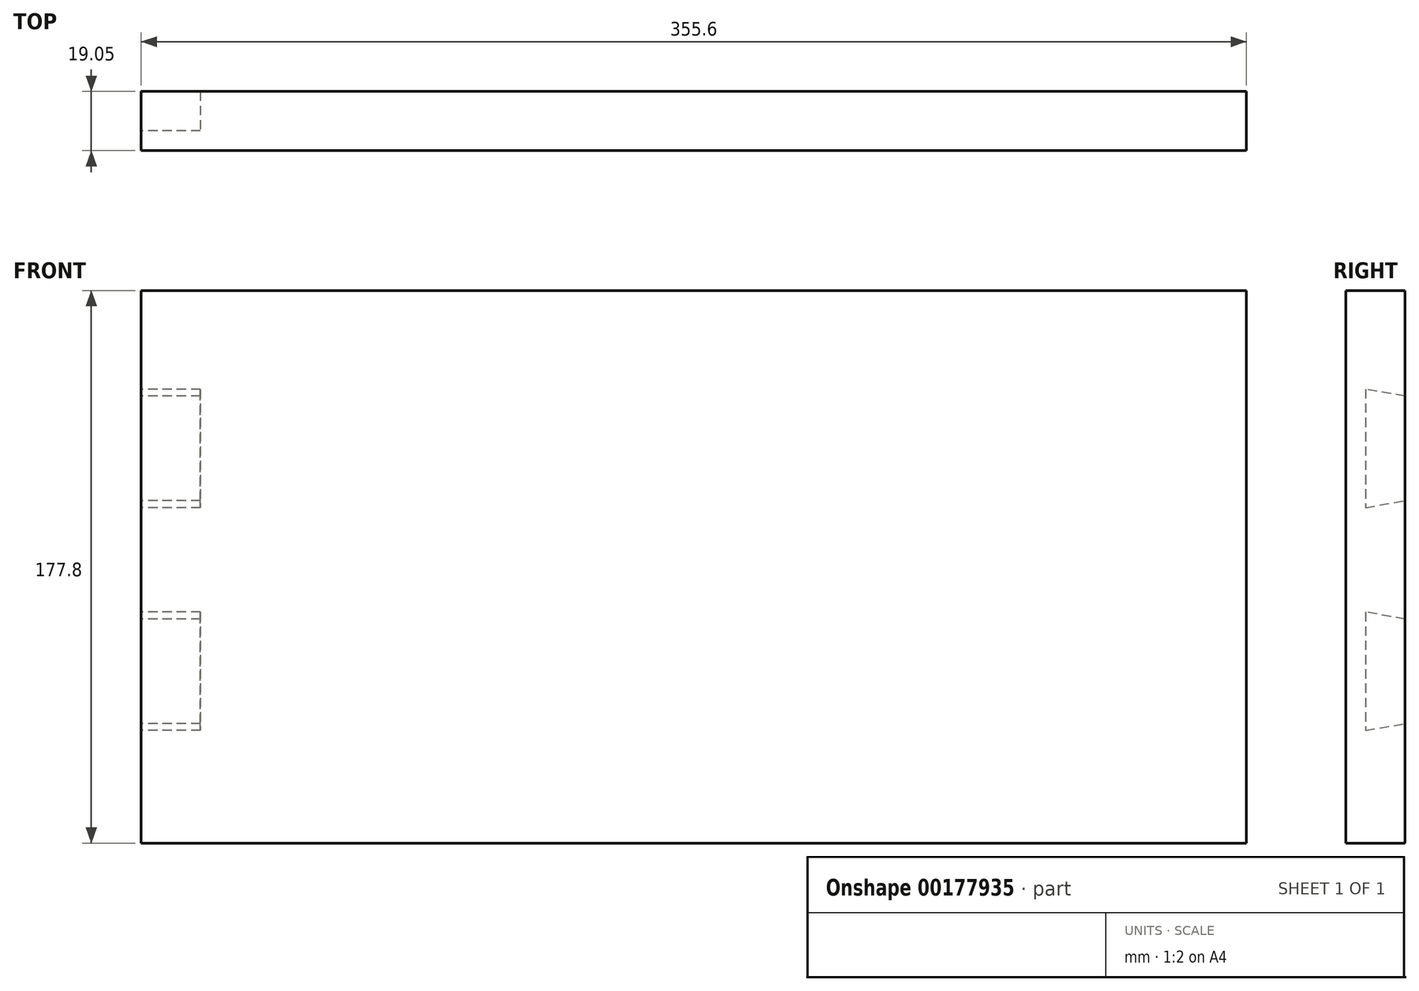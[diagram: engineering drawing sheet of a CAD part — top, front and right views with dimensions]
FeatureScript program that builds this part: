
annotation { "Feature Type Name" : "Feature", "Feature Type Description" : "" }
export const myFeature = defineFeature(function(context is Context, id is Id, definition is map)
    precondition{}
    {
        {
            var Q0;
            Q0=qCreatedBy(makeId("Front.planeOp"),FACE);
            var sketch = newSketch(context, id + "F0", { "sketchPlane" : qUnion([Q0])});
            skLineSegment(sketch, "E0.bottom", {"start": v(0, 0) * mm, "end": v(355.6, 0) * mm});
            skLineSegment(sketch, "E0.top", {"start": v(0, 177.8) * mm, "end": v(355.6, 177.8) * mm});
            skLineSegment(sketch, "E0.left", {"start": v(0, 0) * mm, "end": v(0, 177.8) * mm});
            skLineSegment(sketch, "E0.right", {"start": v(355.6, 0) * mm, "end": v(355.6, 177.8) * mm});
            skSolve(sketch);
        }
        {
            var Q0;
            Q0=makeQuery(id+"F0.imprint","IMPRINT",FACE,{"disambiguationData":[TD([[makeQuery(id+"F0.imprint","IMPRINT",EDGE,{"derivedFrom":sQuery(id+"F0.wireOp",EDGE,"E0.bottom")}),1.0]])]});
            extrude(context, id + "F1", {"entities" : qUnion([Q0]), "depth" : 19.05 * mm});
        }
        {
            var Q0;
            Q0=qCreatedBy(makeId("Right.planeOp"),FACE);
            var sketch = newSketch(context, id + "F2", { "sketchPlane" : qUnion([Q0])});
            skLineSegment(sketch, "E1", {"start": v(-12.7, 146.05) * mm, "end": v(-12.7, 107.95) * mm});
            skLineSegment(sketch, "E2", {"start": v(-12.7, 107.95) * mm, "end": v(0, 110.19) * mm});
            skLineSegment(sketch, "E3", {"start": v(0, 110.19) * mm, "end": v(0, 143.81) * mm});
            skLineSegment(sketch, "E4", {"start": v(0, 143.81) * mm, "end": v(-12.7, 146.05) * mm});
            skLineSegment(sketch, "E5", {"start": v(0, 72.09) * mm, "end": v(-12.7, 74.33) * mm});
            skLineSegment(sketch, "E6", {"start": v(-12.7, 74.33) * mm, "end": v(-12.7, 36.23) * mm});
            skLineSegment(sketch, "E7", {"start": v(-12.7, 36.23) * mm, "end": v(0, 38.47) * mm});
            skLineSegment(sketch, "E8", {"start": v(0, 38.47) * mm, "end": v(0, 72.09) * mm});
            skSolve(sketch);
        }
        {
            var Q0;
            Q0=makeQuery(id+"F2.imprint","IMPRINT",FACE,{"disambiguationData":[TD([[makeQuery(id+"F2.imprint","IMPRINT",EDGE,{"derivedFrom":sQuery(id+"F2.wireOp",EDGE,"E1")}),1.0]])]});
            var Q1;
            Q1=makeQuery(id+"F2.imprint","IMPRINT",FACE,{"disambiguationData":[TD([[makeQuery(id+"F2.imprint","IMPRINT",EDGE,{"derivedFrom":sQuery(id+"F2.wireOp",EDGE,"E5")}),1.0]])]});
            extrude(context, id + "F3", {"entities" : qUnion([Q0, Q1]), "operationType" : NewBodyOperationType.REMOVE, "depth" : 19.05 * mm});
        }
    });
